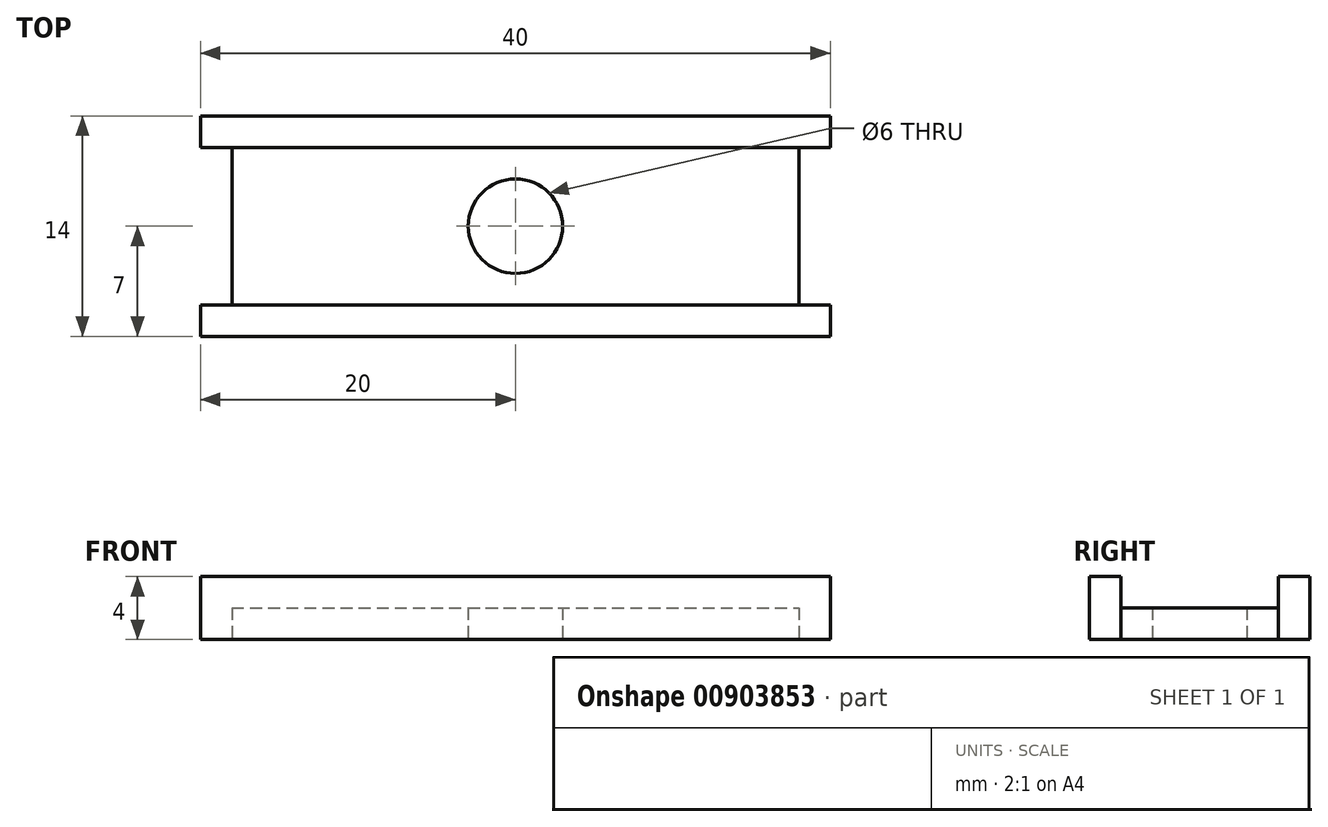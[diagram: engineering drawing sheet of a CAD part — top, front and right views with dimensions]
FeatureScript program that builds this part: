
annotation { "Feature Type Name" : "Feature", "Feature Type Description" : "" }
export const myFeature = defineFeature(function(context is Context, id is Id, definition is map)
    precondition{}
    {
        {
            var Q0;
            Q0=qCreatedBy(makeId("Top.planeOp"),FACE);
            var sketch = newSketch(context, id + "F0", { "sketchPlane" : qUnion([Q0])});
            skLineSegment(sketch, "E0.bottom", {"start": v(-20, 7) * mm, "end": v(20, 7) * mm});
            skLineSegment(sketch, "E0.top", {"start": v(-20, -7) * mm, "end": v(20, -7) * mm});
            skLineSegment(sketch, "E0.left", {"start": v(-20, 7) * mm, "end": v(-20, -7) * mm});
            skLineSegment(sketch, "E0.right", {"start": v(20, 7) * mm, "end": v(20, -7) * mm});
            skPoint(sketch, "E0.middle", {"position": v(0, 0) * mm});
            skLineSegment(sketch, "E1.0", {"start": v(-18, 5) * mm, "end": v(18, 5) * mm});
            skLineSegment(sketch, "E1.1", {"start": v(-18, 5) * mm, "end": v(-18, -5) * mm});
            skLineSegment(sketch, "E1.2", {"start": v(-18, -5) * mm, "end": v(18, -5) * mm});
            skLineSegment(sketch, "E1.3", {"start": v(18, 5) * mm, "end": v(18, -5) * mm});
            skLineSegment(sketch, "E2", {"start": v(-20, 5) * mm, "end": v(20, 5) * mm});
            skLineSegment(sketch, "E3", {"start": v(18, -5) * mm, "end": v(20, -5) * mm});
            skLineSegment(sketch, "E4", {"start": v(20, -5) * mm, "end": v(-20, -5) * mm});
            skSolve(sketch);
        }
        {
            var Q0;
            {var subQ0=sQuery(id+"F0.wireOp",EDGE,"E1.1");Q0=makeQuery(id+"F0.imprint","IMPRINT",FACE,{"disambiguationData":[TD([[makeQuery(id+"F0.imprint","IMPRINT",EDGE,{"derivedFrom":subQ0}),1.0]])]});}
            var Q1;
            {var subQ1=sQuery(id+"F0.wireOp",EDGE,"E0.bottom");Q1=makeQuery(id+"F0.imprint","IMPRINT",FACE,{"disambiguationData":[TD([[makeQuery(id+"F0.imprint","IMPRINT",EDGE,{"derivedFrom":subQ1}),-1.0]])]});}
            var Q2;
            {var subQ4=sQuery(id+"F0.wireOp",EDGE,"E0.top");Q2=makeQuery(id+"F0.imprint","IMPRINT",FACE,{"disambiguationData":[TD([[makeQuery(id+"F0.imprint","IMPRINT",EDGE,{"derivedFrom":subQ4}),1.0]])]});}
            extrude(context, id + "F1", {"entities" : qUnion([Q0, Q1, Q2]), "depth" : 2 * mm, "offsetDistance" : 25 * mm});
        }
        {
            var Q0;
            {var subQ1=sQuery(id+"F0.wireOp",EDGE,"E0.bottom");Q0=makeQuery(id+"F0.imprint","IMPRINT",FACE,{"disambiguationData":[TD([[makeQuery(id+"F0.imprint","IMPRINT",EDGE,{"derivedFrom":subQ1}),-1.0]])]});}
            var Q1;
            {var subQ4=sQuery(id+"F0.wireOp",EDGE,"E0.top");Q1=makeQuery(id+"F0.imprint","IMPRINT",FACE,{"disambiguationData":[TD([[makeQuery(id+"F0.imprint","IMPRINT",EDGE,{"derivedFrom":subQ4}),1.0]])]});}
            extrude(context, id + "F2", {"entities" : qUnion([Q0, Q1]), "operationType" : NewBodyOperationType.ADD, "depth" : 4 * mm, "offsetDistance" : 25 * mm});
        }
        {
            var Q0;
            Q0=makeQuery(id+"F1.opExtrude","CAP_FACE",FACE,{"disambiguationData":[OSD([sQuery(id+"F0.wireOp",EDGE,"E0.bottom"),sQuery(id+"F0.wireOp",EDGE,"E0.top"),sQuery(id+"F0.wireOp",EDGE,"E0.left"),sQuery(id+"F0.wireOp",EDGE,"E0.right"),sQuery(id+"F0.wireOp",EDGE,"E1.1"),sQuery(id+"F0.wireOp",EDGE,"E1.3"),sQuery(id+"F0.wireOp",EDGE,"E2"),sQuery(id+"F0.wireOp",EDGE,"E4")])],"isStart":true});
            var sketch = newSketch(context, id + "F3", { "sketchPlane" : qUnion([Q0])});
            skPoint(sketch, "E5", {"position": v(0, 0) * mm});
            skSolve(sketch);
        }
        {
            var Q0;
            Q0=sQuery(id+"F3.wireOp",VERTEX,"E5");
            var Q1;
            Q1=makeQuery(id+"F1.opExtrude","SWEPT_BODY",BODY,{"disambiguationData":[OSD([sQuery(id+"F0.wireOp",EDGE,"E0.bottom"),sQuery(id+"F0.wireOp",EDGE,"E0.top"),sQuery(id+"F0.wireOp",EDGE,"E0.left"),sQuery(id+"F0.wireOp",EDGE,"E0.right"),sQuery(id+"F0.wireOp",EDGE,"E1.1"),sQuery(id+"F0.wireOp",EDGE,"E1.3"),sQuery(id+"F0.wireOp",EDGE,"E2"),sQuery(id+"F0.wireOp",EDGE,"E4")])]});
            hole(context, id + "F4", {"style" : HoleStyle.SIMPLE, "endStyle" : HoleEndStyle.BLIND, "holeDiameter" : 6 * mm, "majorDiameter" : 5 * mm, "holeDepth" : 2 * mm, "isTappedThrough" : true, "tappedDepth" : 12 * mm, "tapClearance" : 3, "locations" : qUnion([Q0]), "scope" : qUnion([Q1])});
        }
    });
